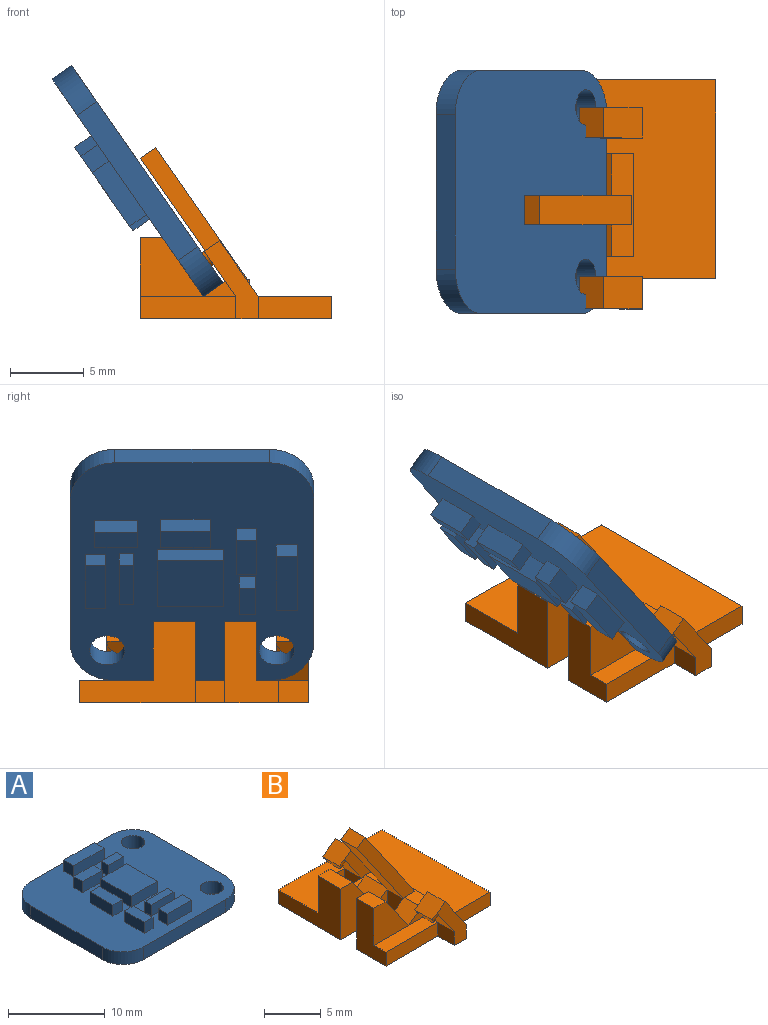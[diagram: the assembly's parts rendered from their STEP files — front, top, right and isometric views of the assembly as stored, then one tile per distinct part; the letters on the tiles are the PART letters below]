
ASSEMBLY  parts=2 mates=1
PART A: 52 faces, bbox 18x16.5x3 mm
  f0: plane 18x16.5mm, normal (0,0,1), area 234.3mm2, adj f1,f2,f3,f4,f5,f6,f8,f9
  f1: plane 12x1.6mm, normal (0,-1,0), area 19.2mm2, adj f0,f7,f8,f11
  f2: plane 10.5x1.6mm, normal (1,0,0), area 16.8mm2, adj f0,f7,f8,f9
  f3: plane 12x1.6mm, normal (0,1,0), area 19.2mm2, adj f0,f7,f9,f10
  f4: cylinder r=1.2mm len=2.4mm, axis (0,0,-1), area 12.1mm2, adj f0,f7
  f5: cylinder r=1.2mm len=2.4mm, axis (0,0,-1), area 12.1mm2, adj f0,f7
  f6: plane 10.5x1.6mm, normal (-1,0,0), area 16.8mm2, adj f0,f7,f10,f11
  f7: plane 18x16.5mm, normal (0,0,-1), area 280.2mm2, adj f1,f2,f3,f4,f5,f6,f8,f9
  f8: cylinder r=3mm len=3mm, axis (0,0,1), area 7.5mm2, adj f0,f1,f2,f7
  f9: cylinder r=3mm len=3mm, axis (0,0,-1), area 7.5mm2, adj f0,f2,f3,f7
  f10: cylinder r=3mm len=3mm, axis (0,0,1), area 7.5mm2, adj f0,f3,f6,f7
  f11: cylinder r=3mm len=3mm, axis (0,0,-1), area 7.5mm2, adj f0,f1,f6,f7
  f12: plane 3.79x1.4mm, normal (0,1,0), area 5.3mm2, adj f0,f13,f15,f16
  f13: plane 4.48x1.4mm, normal (-1,0,0), area 6.3mm2, adj f0,f12,f14,f16
  f14: plane 3.79x1.4mm, normal (0,-1,0), area 5.3mm2, adj f0,f13,f15,f16
  f15: plane 4.48x1.4mm, normal (1,0,0), area 6.3mm2, adj f0,f12,f14,f16
  f16: plane 4.48x3.79mm, normal (0,0,1), area 17mm2, adj f12,f13,f14,f15
  f17: plane 4.45x1.4mm, normal (0,1,0), area 6.2mm2, adj f0,f18,f20,f21
  f18: plane 1.45x1.4mm, normal (-1,0,0), area 2mm2, adj f0,f17,f19,f21
  f19: plane 4.45x1.4mm, normal (0,-1,0), area 6.2mm2, adj f0,f18,f20,f21
  f20: plane 1.45x1.4mm, normal (1,0,0), area 2mm2, adj f0,f17,f19,f21
  f21: plane 4.45x1.45mm, normal (0,0,1), area 6.4mm2, adj f17,f18,f19,f20
  f22: plane 2.21x1.4mm, normal (0,1,0), area 3.1mm2, adj f0,f23,f25,f26
  f23: plane 1.4x1.1mm, normal (-1,0,0), area 1.5mm2, adj f0,f22,f24,f26
  f24: plane 2.21x1.4mm, normal (0,-1,0), area 3.1mm2, adj f0,f23,f25,f26
  f25: plane 1.4x1.1mm, normal (1,0,0), area 1.5mm2, adj f0,f22,f24,f26
  f26: plane 2.21x1.1mm, normal (0,0,1), area 2.4mm2, adj f22,f23,f24,f25
  f27: plane 2.86x1.4mm, normal (0,1,0), area 4mm2, adj f0,f28,f30,f31
  f28: plane 1.4x1.31mm, normal (-1,0,0), area 1.8mm2, adj f0,f27,f29,f31
  f29: plane 2.86x1.4mm, normal (0,-1,0), area 4mm2, adj f0,f28,f30,f31
  f30: plane 1.4x1.31mm, normal (1,0,0), area 1.8mm2, adj f0,f27,f29,f31
  f31: plane 2.86x1.31mm, normal (0,0,1), area 3.7mm2, adj f27,f28,f29,f30
  f32: plane 3.27x1.4mm, normal (0,1,0), area 4.6mm2, adj f0,f33,f35,f36
  f33: plane 1.4x0.97mm, normal (-1,0,0), area 1.4mm2, adj f0,f32,f34,f36
  f34: plane 3.27x1.4mm, normal (0,-1,0), area 4.6mm2, adj f0,f33,f35,f36
  f35: plane 1.4x0.97mm, normal (1,0,0), area 1.4mm2, adj f0,f32,f34,f36
  f36: plane 3.27x0.97mm, normal (0,0,1), area 3.2mm2, adj f32,f33,f34,f35
  f37: plane 3.51x1.4mm, normal (0,1,0), area 4.9mm2, adj f0,f38,f40,f41
  f38: plane 1.4x1.38mm, normal (-1,0,0), area 1.9mm2, adj f0,f37,f39,f41
  f39: plane 3.51x1.4mm, normal (0,-1,0), area 4.9mm2, adj f0,f38,f40,f41
  f40: plane 1.4x1.38mm, normal (1,0,0), area 1.9mm2, adj f0,f37,f39,f41
  f41: plane 3.51x1.38mm, normal (0,0,1), area 4.8mm2, adj f37,f38,f39,f40
  f42: plane 1.4x1.28mm, normal (0,1,0), area 1.8mm2, adj f0,f43,f45,f46
  f43: plane 2.89x1.4mm, normal (-1,0,0), area 4.1mm2, adj f0,f42,f44,f46
  f44: plane 1.4x1.28mm, normal (0,-1,0), area 1.8mm2, adj f0,f43,f45,f46
  f45: plane 2.89x1.4mm, normal (1,0,0), area 4.1mm2, adj f0,f42,f44,f46
  f46: plane 2.89x1.28mm, normal (0,0,1), area 3.7mm2, adj f42,f43,f44,f45
  f47: plane 1.4x1.38mm, normal (0,1,0), area 1.9mm2, adj f0,f48,f50,f51
  f48: plane 3.34x1.4mm, normal (-1,0,0), area 4.7mm2, adj f0,f47,f49,f51
  f49: plane 1.4x1.38mm, normal (0,-1,0), area 1.9mm2, adj f0,f48,f50,f51
  f50: plane 3.34x1.4mm, normal (1,0,0), area 4.7mm2, adj f0,f47,f49,f51
  f51: plane 3.34x1.38mm, normal (0,0,1), area 4.6mm2, adj f47,f48,f49,f50
PART B: 49 faces, bbox 13x15.6x11.6 mm
  f0: plane 6.48x1.5mm, normal (0,-1,0), area 9.7mm2, adj f2,f6,f7,f48
  f1: plane 4x2.79mm, normal (0.82,0,0.57), area 10.5mm2, adj f3,f8,f16,f46
  f2: plane 5.5x3.65mm, normal (-1,0,0), area 14.1mm2, adj f0,f3,f6,f7,f16,f46
  f3: plane 2.15x1.5mm, normal (0,0,1), area 3.2mm2, adj f1,f2,f16,f46
  f4: plane 7.85x5.5mm, normal (-1,0,0), area 23.2mm2, adj f6,f7,f13,f15,f17,f45
  f5: plane 2.85x1.64mm, normal (-0.57,0,0.82), area 5.7mm2, adj f14,f19,f21,f37,f45
  f6: plane 13.5x13mm, normal (0,0,1), area 114.3mm2, adj f0,f2,f4,f9,f11,f12,f13,f16
  f7: plane 15.55x13mm, normal (0,0,-1), area 161.2mm2, adj f0,f2,f4,f11,f12,f13,f30,f39
  f8: plane 2.15x1.64mm, normal (-0.57,0,0.82), area 4.3mm2, adj f1,f19,f20,f38,f46
  f9: plane 3.08x2.2mm, normal (-0.82,0,-0.57), area 6.4mm2, adj f6,f30,f31,f32,f48
  f10: plane 3.07x2.14mm, normal (-0.82,0,-0.57), area 6.1mm2, adj f24,f25,f26,f43
  f11: plane 5x1.5mm, normal (0,-1,0), area 7.5mm2, adj f6,f7,f12,f47
  f12: plane 13.5x1.5mm, normal (1,0,0), area 20.2mm2, adj f6,f7,f11,f13
  f13: plane 13x1.5mm, normal (0,1,0), area 19.5mm2, adj f4,f6,f7,f12
  f14: plane 4x2.85mm, normal (0.82,0,0.57), area 13.9mm2, adj f5,f15,f17,f45
  f15: plane 2.85x1.5mm, normal (0,0,1), area 4.3mm2, adj f4,f14,f17,f45
  f16: plane 4.29x4mm, normal (0,-1,0), area 11.6mm2, adj f1,f2,f3,f6
  f17: plane 4.29x4mm, normal (0,1,0), area 11.6mm2, adj f4,f6,f14,f15
  f18: plane 7x1.14mm, normal (1,0,0), area 8mm2, adj f6,f19,f20,f21
  f19: plane 7x1.5mm, normal (0,0,1), area 7.8mm2, adj f5,f8,f18,f20,f21,f36,f37,f38
  f20: plane 3.14x1.14mm, normal (0,-1,0), area 2.7mm2, adj f6,f8,f18,f19
  f21: plane 3.14x1.14mm, normal (0,1,0), area 2.7mm2, adj f5,f6,f18,f19
  f22: plane 2.1x1.64mm, normal (-0.57,0,0.82), area 4.2mm2, adj f23,f24,f25,f26,f27
  f23: plane 3.79x2.64mm, normal (0.82,0,0.57), area 9.7mm2, adj f6,f22,f24,f25
  f24: plane 3.79x3.67mm, normal (0,-1,0), area 5.2mm2, adj f6,f10,f22,f23,f42,f43
  f25: plane 3.79x3.67mm, normal (0,1,0), area 5.2mm2, adj f6,f10,f22,f23,f42,f43
  f26: cylinder r=1.05mm len=2.1mm, axis (0.82,0,0.57), area 2.5mm2, adj f10,f22,f27
  f27: plane 2.1x0.86mm, normal (-0.82,0,-0.57), area 1.7mm2, adj f22,f26
  f28: plane 3.79x2.64mm, normal (0.82,0,0.57), area 10.2mm2, adj f6,f29,f30,f31,f47
  f29: plane 2.2x1.64mm, normal (-0.57,0,0.82), area 4.4mm2, adj f28,f30,f31,f32,f33
  f30: plane 5.29x3.67mm, normal (0,-1,0), area 7.5mm2, adj f7,f9,f28,f29,f47,f48
  f31: plane 3.79x3.67mm, normal (0,1,0), area 5.2mm2, adj f6,f9,f28,f29
  f32: cylinder r=1.1mm len=2.2mm, axis (0.82,0,0.57), area 2.6mm2, adj f9,f29,f33
  f33: plane 2.2x0.9mm, normal (-0.82,0,-0.57), area 1.9mm2, adj f29,f32
  f34: plane 8.33x5.8mm, normal (-0.82,0,-0.57), area 20.3mm2, adj f35,f37,f38,f44
  f35: plane 2x1.03mm, normal (-0.57,0,0.82), area 2.5mm2, adj f34,f36,f37,f38
  f36: plane 8.96x6.24mm, normal (0.82,0,0.57), area 21.8mm2, adj f19,f35,f37,f38
  f37: plane 9.05x7.27mm, normal (0,1,0), area 13.1mm2, adj f5,f19,f34,f35,f36
  f38: plane 9.05x7.27mm, normal (0,-1,0), area 13.1mm2, adj f8,f19,f34,f35,f36
  f39: plane 2.76x1.5mm, normal (0,-1,0), area 4.1mm2, adj f6,f7,f40,f42
  f40: plane 2.1x1.5mm, normal (1,0,0), area 3.2mm2, adj f6,f7,f39,f41
  f41: plane 2.76x1.5mm, normal (0,1,0), area 4.1mm2, adj f6,f7,f40,f42
  f42: plane 2.1x1.51mm, normal (-1,0,0), area 3.2mm2, adj f7,f24,f25,f39,f41,f43
  f43: plane 2.1x0.01mm, normal (0,0,-1), area 0mm2, adj f10,f24,f25,f42
  f44: plane 2.56x2mm, normal (-1,0,0), area 5.1mm2, adj f7,f34,f45,f46
  f45: plane 5.8x5.5mm, normal (0,-1,0), area 21.1mm2, adj f4,f5,f7,f14,f15,f44
  f46: plane 5.8x5.5mm, normal (0,1,0), area 21.1mm2, adj f1,f2,f3,f7,f8,f44
  f47: plane 2.05x1.5mm, normal (1,0,0), area 3.1mm2, adj f7,f11,f28,f30
  f48: plane 2.05x1.5mm, normal (-1,0,0), area 3.1mm2, adj f0,f7,f9,f30
PLACE A rot(axis=(0.89,0,-0.46),180deg) t=(-6.97,-2.15,9.05)mm
PLACE B t=(-0.92,-1.27,-0.75)mm
MATE fastened A.f0 <-> B.f14  axis (-0.82,0,-0.57) through (-3.14,-2.15,0.75)mm
